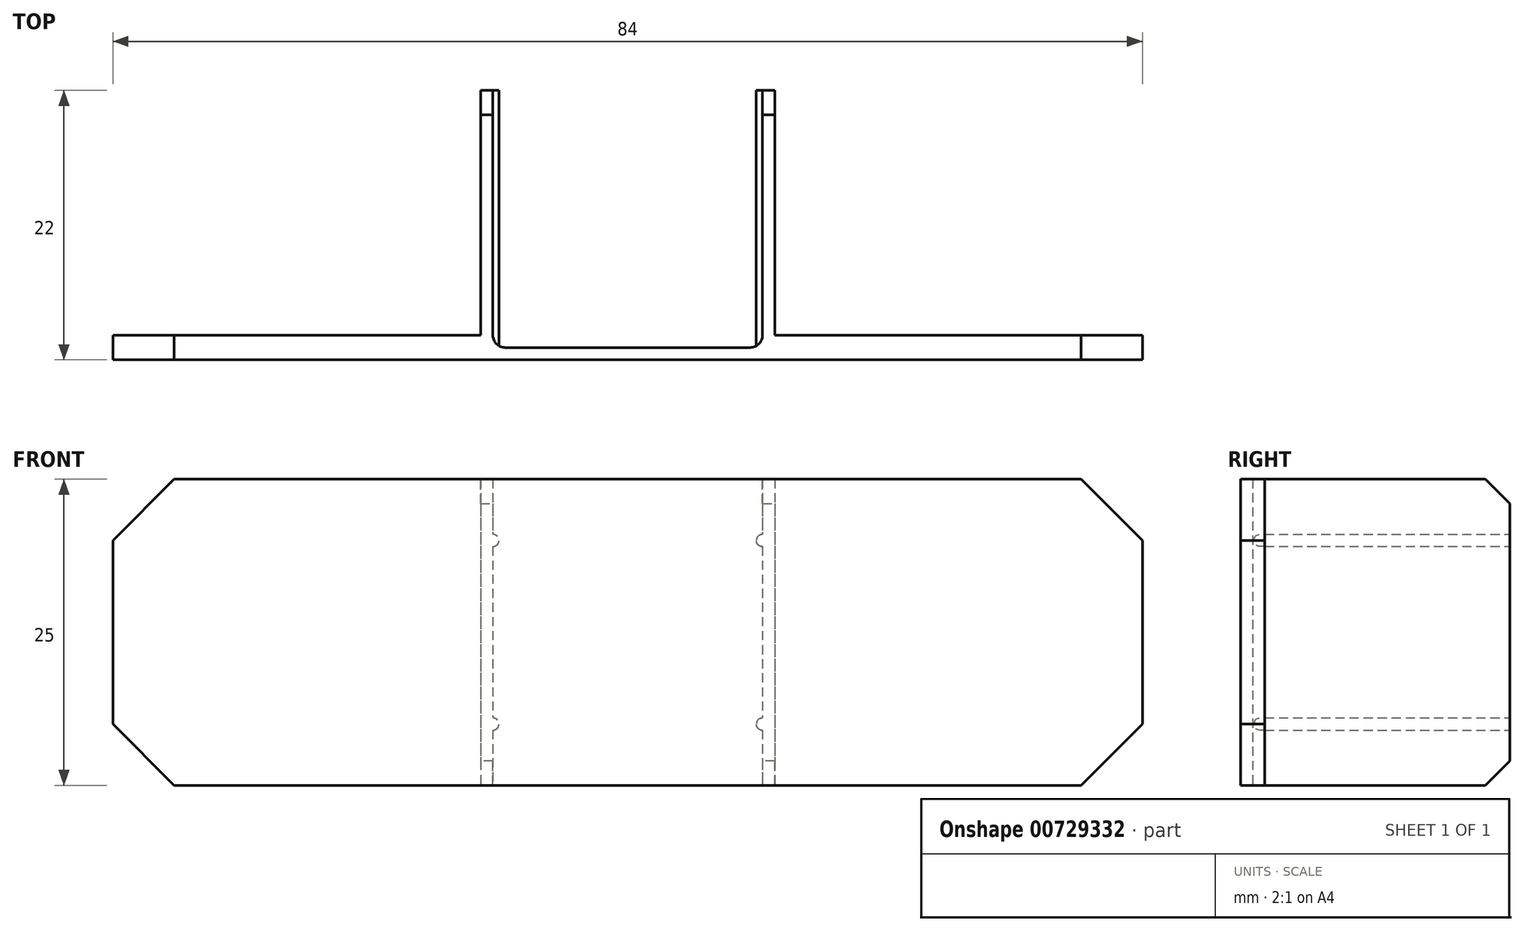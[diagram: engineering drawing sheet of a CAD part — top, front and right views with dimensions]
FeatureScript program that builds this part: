
annotation { "Feature Type Name" : "Feature", "Feature Type Description" : "" }
export const myFeature = defineFeature(function(context is Context, id is Id, definition is map)
    precondition{}
    {
        {
            var Q0;
            Q0=qCreatedBy(makeId("Top.planeOp"),FACE);
            var sketch = newSketch(context, id + "F0", { "sketchPlane" : qUnion([Q0])});
            skLineSegment(sketch, "E0.bottom", {"start": v(0, 0) * mm, "end": v(-11, 0) * mm});
            skLineSegment(sketch, "E0.top", {"start": v(0, 1) * mm, "end": v(-11, 1) * mm});
            skLineSegment(sketch, "E0.left", {"start": v(0, 0) * mm, "end": v(0, 1) * mm});
            skLineSegment(sketch, "E1.bottom", {"start": v(0, 0) * mm, "end": v(1, 0) * mm});
            skLineSegment(sketch, "E1.top", {"start": v(0, 22) * mm, "end": v(1, 22) * mm});
            skLineSegment(sketch, "E1.left", {"start": v(0, 0) * mm, "end": v(0, 22) * mm});
            skLineSegment(sketch, "E1.right", {"start": v(1, 0) * mm, "end": v(1, 22) * mm});
            skLineSegment(sketch, "E2", {"start": v(-11, 1) * mm, "end": v(-11, 0) * mm});
            skLineSegment(sketch, "E3.bottom", {"start": v(1, 0) * mm, "end": v(31, 0) * mm});
            skLineSegment(sketch, "E3.top", {"start": v(1, 2) * mm, "end": v(31, 2) * mm});
            skLineSegment(sketch, "E3.left", {"start": v(1, 0) * mm, "end": v(1, 2) * mm});
            skLineSegment(sketch, "E3.right", {"start": v(31, 0) * mm, "end": v(31, 2) * mm});
            skSolve(sketch);
        }
        {
            var Q0;
            Q0=makeQuery(id+"F0.imprint","IMPRINT",FACE,{"disambiguationData":[TD([[makeQuery(id+"F0.imprint","IMPRINT",EDGE,{"derivedFrom":sQuery(id+"F0.wireOp",EDGE,"E3.bottom")}),1.0]])]});
            var Q1;
            {var subQ3=sQuery(id+"F0.wireOp",EDGE,"E1.bottom");Q1=makeQuery(id+"F0.imprint","IMPRINT",FACE,{"disambiguationData":[TD([[makeQuery(id+"F0.imprint","IMPRINT",EDGE,{"derivedFrom":subQ3}),1.0]])]});}
            var Q2;
            {var subQ0=sQuery(id+"F0.wireOp",EDGE,"E0.bottom");Q2=makeQuery(id+"F0.imprint","IMPRINT",FACE,{"disambiguationData":[TD([[makeQuery(id+"F0.imprint","IMPRINT",EDGE,{"derivedFrom":subQ0}),-1.0]])]});}
            extrude(context, id + "F1", {"entities" : qUnion([Q0, Q1, Q2]), "depth" : 25 * mm, "offsetDistance" : 25 * mm});
        }
        {
            var Q0;
            Q0=makeQuery(id+"F1.opExtrude","CAP_EDGE",EDGE,{"disambiguationData":[OSD([sQuery(id+"F0.wireOp",EDGE,"E3.right")])],"isStart":true});
            var Q1;
            Q1=makeQuery(id+"F1.opExtrude","CAP_EDGE",EDGE,{"disambiguationData":[OSD([sQuery(id+"F0.wireOp",EDGE,"E3.right")])],"isStart":false});
            chamfer(context, id + "F2", {"entities" : qUnion([Q0, Q1]), "width" : 5 * mm, "tangentPropagation" : true});
        }
        {
            var Q0;
            Q0=makeQuery(id+"F1.opExtrude","SWEPT_EDGE",EDGE,{"disambiguationData":[OSD([sQuery(id+"F0.wireOp",EDGE,"E0.top"),sQuery(id+"F0.wireOp",EDGE,"E1.left")])]});
            fillet(context, id + "F3", {"entities" : qUnion([Q0]), "radius" : 1 * mm, "tangentPropagation" : true, "allowEdgeOverflow" : false});
        }
        {
            var Q0;
            Q0=makeQuery(id+"F1.opExtrude","SWEPT_FACE",FACE,{"disambiguationData":[OSD([sQuery(id+"F0.wireOp",EDGE,"E1.top")])]});
            var sketch = newSketch(context, id + "F4", { "sketchPlane" : qUnion([Q0])});
            skCircle(sketch, "E4", {"center": v(0, 20) * mm, "radius": 0.5 * mm});
            skCircle(sketch, "E5", {"center": v(0, 5) * mm, "radius": 0.5 * mm});
            skSolve(sketch);
        }
        {
            var Q0;
            {var subQ0=sQuery(id+"F4.wireOp",EDGE,"E5");var subQ1=makeQuery(id+"F1.opExtrude","SWEPT_EDGE",EDGE,{"disambiguationData":[OSD([sQuery(id+"F0.wireOp",EDGE,"E1.top"),sQuery(id+"F0.wireOp",EDGE,"E1.left")])]});var subQ2=makeQuery(id+"F4.imprint","INTERSECT",VERTEX,{"disambiguationData":[OD(0.0)],"derivedFrom":[subQ1,subQ0]});Q0=makeQuery(id+"F4.imprint","IMPRINT",FACE,{"disambiguationData":[TD([[makeQuery(id+"F4.imprint","IMPRINT",EDGE,{"disambiguationData":[TD([[subQ2,-1.0]])],"derivedFrom":subQ0}),1.0]])]});}
            var Q1;
            {var subQ0=sQuery(id+"F4.wireOp",EDGE,"E4");var subQ1=makeQuery(id+"F1.opExtrude","SWEPT_EDGE",EDGE,{"disambiguationData":[OSD([sQuery(id+"F0.wireOp",EDGE,"E1.top"),sQuery(id+"F0.wireOp",EDGE,"E1.left")])]});var subQ2=makeQuery(id+"F4.imprint","INTERSECT",VERTEX,{"disambiguationData":[OD(0.0)],"derivedFrom":[subQ1,subQ0]});Q1=makeQuery(id+"F4.imprint","IMPRINT",FACE,{"disambiguationData":[TD([[makeQuery(id+"F4.imprint","IMPRINT",EDGE,{"disambiguationData":[TD([[subQ2,1.0]])],"derivedFrom":subQ0}),1.0]])]});}
            extrude(context, id + "F5", {"entities" : qUnion([Q0, Q1]), "operationType" : NewBodyOperationType.ADD, "endBound" : BoundingType.UP_TO_NEXT, "oppositeDirection" : true, "depth" : 25 * mm, "offsetDistance" : 25 * mm});
        }
        {
            var Q0;
            Q0=makeQuery(id+"F1.opExtrude","SWEPT_BODY",BODY,{"disambiguationData":[OSD([sQuery(id+"F0.wireOp",EDGE,"E0.bottom"),sQuery(id+"F0.wireOp",EDGE,"E0.top"),sQuery(id+"F0.wireOp",EDGE,"E1.bottom"),sQuery(id+"F0.wireOp",EDGE,"E1.top"),sQuery(id+"F0.wireOp",EDGE,"E1.left"),sQuery(id+"F0.wireOp",EDGE,"E1.right"),sQuery(id+"F0.wireOp",EDGE,"E2"),sQuery(id+"F0.wireOp",EDGE,"E3.bottom"),sQuery(id+"F0.wireOp",EDGE,"E3.top"),sQuery(id+"F0.wireOp",EDGE,"E3.right")])]});
            var Q1;
            Q1=makeQuery(id+"F1.opExtrude","SWEPT_FACE",FACE,{"disambiguationData":[OSD([sQuery(id+"F0.wireOp",EDGE,"E2")])]});
            mirror(context, id + "F6", {"operationType" : NewBodyOperationType.ADD, "entities" : qUnion([Q0]), "mirrorPlane" : qUnion([Q1])});
        }
        {
            var Q0;
            Q0=makeQuery(id+"F6.opPattern","COPY",EDGE,{"derivedFrom":makeQuery(id+"F1.opExtrude","CAP_EDGE",EDGE,{"disambiguationData":[OSD([sQuery(id+"F0.wireOp",EDGE,"E1.top")])],"isStart":false}),"instanceName":"1"});
            var Q1;
            Q1=makeQuery(id+"F6.opPattern","COPY",EDGE,{"derivedFrom":makeQuery(id+"F1.opExtrude","CAP_EDGE",EDGE,{"disambiguationData":[OSD([sQuery(id+"F0.wireOp",EDGE,"E1.top")])],"isStart":true}),"instanceName":"1"});
            var Q2;
            Q2=makeQuery(id+"F1.opExtrude","CAP_EDGE",EDGE,{"disambiguationData":[OSD([sQuery(id+"F0.wireOp",EDGE,"E1.top")])],"isStart":false});
            var Q3;
            Q3=makeQuery(id+"F1.opExtrude","CAP_EDGE",EDGE,{"disambiguationData":[OSD([sQuery(id+"F0.wireOp",EDGE,"E1.top")])],"isStart":true});
            chamfer(context, id + "F7", {"entities" : qUnion([Q0, Q1, Q2, Q3]), "width" : 2 * mm, "tangentPropagation" : true});
        }
    });
